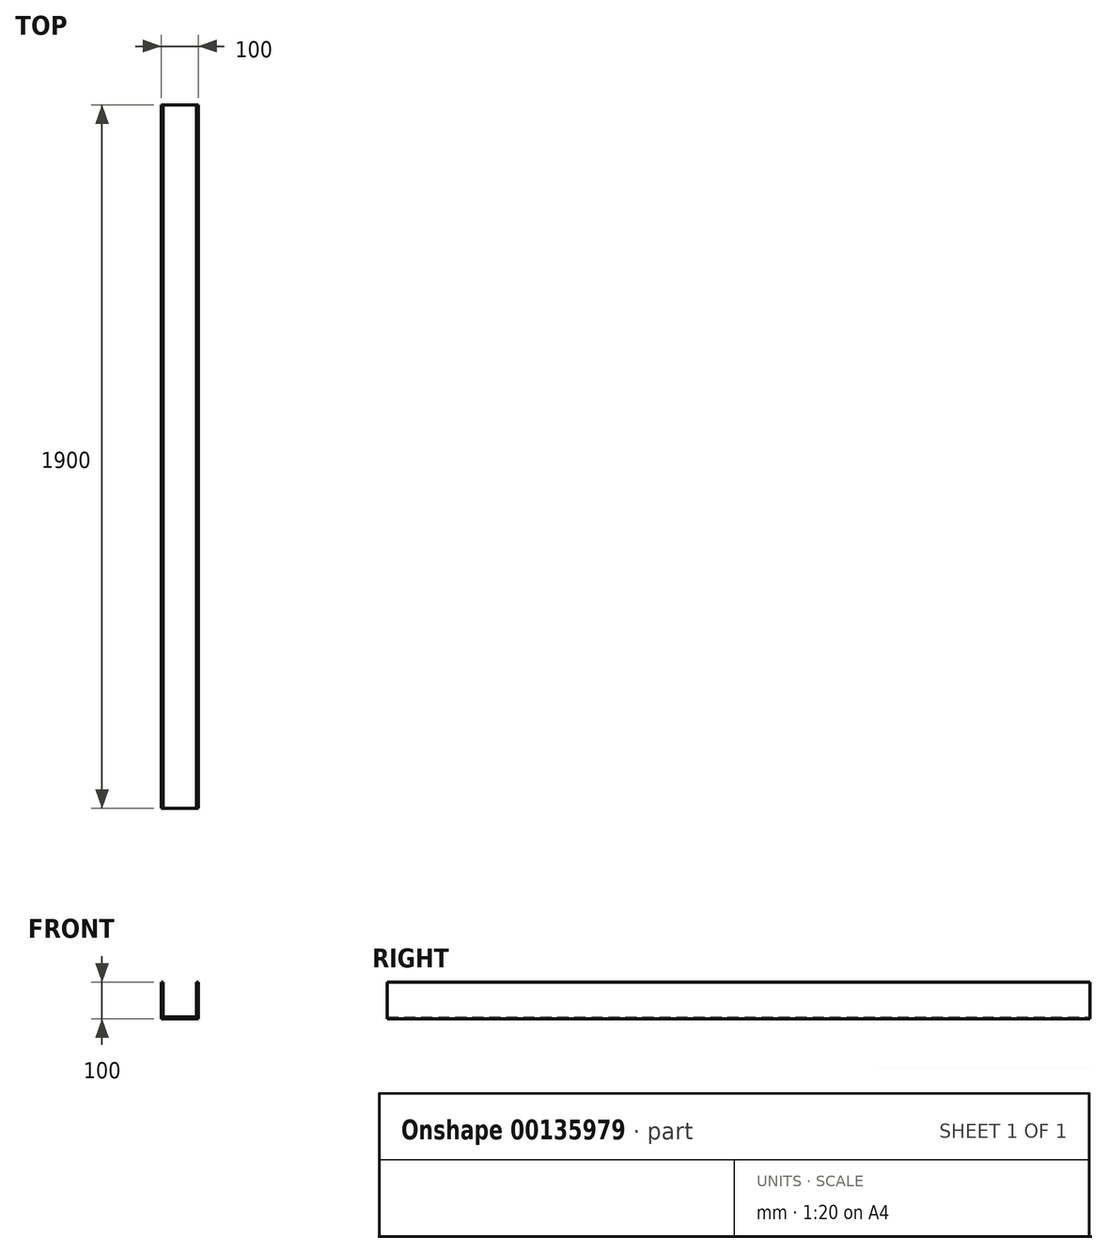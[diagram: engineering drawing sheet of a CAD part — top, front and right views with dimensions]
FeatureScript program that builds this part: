
annotation { "Feature Type Name" : "Feature", "Feature Type Description" : "" }
export const myFeature = defineFeature(function(context is Context, id is Id, definition is map)
    precondition{}
    {
        {
            var Q0;
            Q0=qCreatedBy(makeId("Front.planeOp"),FACE);
            var sketch = newSketch(context, id + "F0", { "sketchPlane" : qUnion([Q0])});
            skLineSegment(sketch, "E0", {"start": v(-50, 50) * mm, "end": v(-50, -50) * mm});
            skLineSegment(sketch, "E1", {"start": v(-50, -50) * mm, "end": v(50, -50) * mm});
            skLineSegment(sketch, "E2", {"start": v(50, -50) * mm, "end": v(50, 50) * mm});
            skLineSegment(sketch, "E3", {"start": v(50, 50) * mm, "end": v(45, 50) * mm});
            skLineSegment(sketch, "E4", {"start": v(45, 50) * mm, "end": v(45, -45) * mm});
            skLineSegment(sketch, "E5", {"start": v(45, -45) * mm, "end": v(-45, -45) * mm});
            skLineSegment(sketch, "E6", {"start": v(-45, -45) * mm, "end": v(-45, 50) * mm});
            skLineSegment(sketch, "E7", {"start": v(-45, 50) * mm, "end": v(-50, 50) * mm});
            skSolve(sketch);
        }
        {
            var Q0;
            Q0=makeQuery(id+"F0.imprint","IMPRINT",FACE,{"disambiguationData":[TD([[makeQuery(id+"F0.imprint","IMPRINT",EDGE,{"derivedFrom":sQuery(id+"F0.wireOp",EDGE,"E0")}),1.0]])]});
            extrude(context, id + "F1", {"entities" : qUnion([Q0]), "endBound" : BoundingType.SYMMETRIC, "depth" : 1900 * mm});
        }
    });
